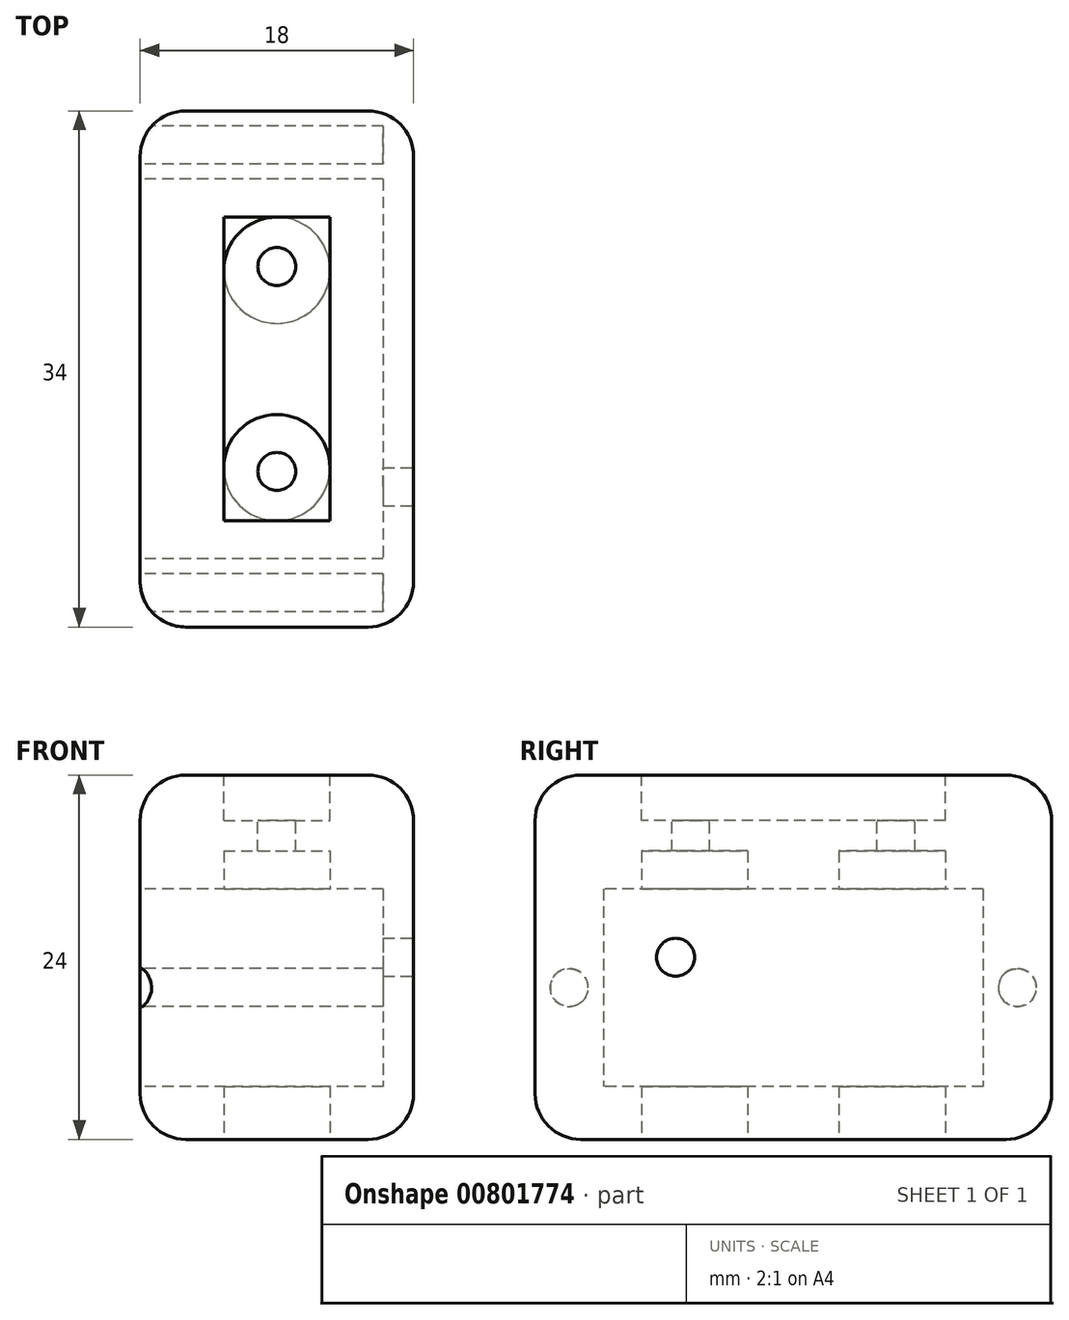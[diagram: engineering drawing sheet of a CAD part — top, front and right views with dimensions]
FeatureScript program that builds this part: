
annotation { "Feature Type Name" : "Feature", "Feature Type Description" : "" }
export const myFeature = defineFeature(function(context is Context, id is Id, definition is map)
    precondition{}
    {
        {
            var Q0;
            Q0=qCreatedBy(makeId("Front.planeOp"),FACE);
            var sketch = newSketch(context, id + "F0", { "sketchPlane" : qUnion([Q0])});
            skLineSegment(sketch, "E0.bottom", {"start": v(-19.6, 6.77) * mm, "end": v(-1.6, 6.77) * mm});
            skLineSegment(sketch, "E0.top", {"start": v(-19.6, -17.23) * mm, "end": v(-1.6, -17.23) * mm});
            skLineSegment(sketch, "E0.left", {"start": v(-19.6, 6.77) * mm, "end": v(-19.6, -17.23) * mm});
            skLineSegment(sketch, "E0.right", {"start": v(-1.6, 6.77) * mm, "end": v(-1.6, -17.23) * mm});
            skSolve(sketch);
        }
        {
            var Q0;
            Q0 = qSketchRegion(id + "F0", true);
            extrude(context, id + "F1", {"entities" : qUnion([Q0]), "depth" : 34 * mm, "offsetDistance" : 25 * mm});
        }
        {
            var Q0;
            Q0=makeQuery(id+"F1.opExtrude","SWEPT_FACE",FACE,{"disambiguationData":[OSD([sQuery(id+"F0.wireOp",EDGE,"E0.left")])]});
            var sketch = newSketch(context, id + "F2", { "sketchPlane" : qUnion([Q0])});
            skLineSegment(sketch, "E1.bottom", {"start": v(4.5, -0.73) * mm, "end": v(29.5, -0.73) * mm});
            skLineSegment(sketch, "E1.top", {"start": v(4.5, -13.73) * mm, "end": v(29.5, -13.73) * mm});
            skLineSegment(sketch, "E1.left", {"start": v(4.5, -0.73) * mm, "end": v(4.5, -13.73) * mm});
            skLineSegment(sketch, "E1.right", {"start": v(29.5, -0.73) * mm, "end": v(29.5, -13.73) * mm});
            skCircle(sketch, "E2", {"center": v(2.25, -7.23) * mm, "radius": 1.25 * mm});
            skPoint(sketch, "E2.centerSnap0", {"position": v(4.5, -7.23) * mm});
            skCircle(sketch, "E3", {"center": v(31.75, -7.23) * mm, "radius": 1.25 * mm});
            skPoint(sketch, "E3.centerSnap0", {"position": v(29.5, -7.23) * mm});
            skSolve(sketch);
        }
        {
            var Q0;
            Q0 = qSketchRegion(id + "F2", true);
            extrude(context, id + "F3", {"entities" : qUnion([Q0]), "operationType" : NewBodyOperationType.REMOVE, "oppositeDirection" : true, "depth" : 16 * mm, "offsetDistance" : 25 * mm});
        }
        {
            var Q0;
            Q0=makeQuery(id+"F1.opExtrude","SWEPT_FACE",FACE,{"disambiguationData":[OSD([sQuery(id+"F0.wireOp",EDGE,"E0.bottom")])]});
            var sketch = newSketch(context, id + "F4", { "sketchPlane" : qUnion([Q0])});
            skLineSegment(sketch, "E4.bottom", {"start": v(-14.1, -7) * mm, "end": v(-7.1, -7) * mm});
            skLineSegment(sketch, "E4.top", {"start": v(-14.1, -27) * mm, "end": v(-7.1, -27) * mm});
            skLineSegment(sketch, "E4.left", {"start": v(-14.1, -7) * mm, "end": v(-14.1, -27) * mm});
            skLineSegment(sketch, "E4.right", {"start": v(-7.1, -7) * mm, "end": v(-7.1, -27) * mm});
            skSolve(sketch);
        }
        {
            var Q0;
            Q0 = qSketchRegion(id + "F4", true);
            extrude(context, id + "F5", {"entities" : qUnion([Q0]), "operationType" : NewBodyOperationType.REMOVE, "oppositeDirection" : true, "depth" : 3 * mm, "offsetDistance" : 25 * mm});
        }
        {
            var Q0;
            Q0=makeQuery(id+"F5.boolean.opBoolean","COPY",FACE,{"derivedFrom":makeQuery(id+"F5.opExtrude","CAP_FACE",FACE,{"disambiguationData":[OSD([sQuery(id+"F4.wireOp",EDGE,"E4.bottom"),sQuery(id+"F4.wireOp",EDGE,"E4.top"),sQuery(id+"F4.wireOp",EDGE,"E4.left"),sQuery(id+"F4.wireOp",EDGE,"E4.right")])],"isStart":false})});
            var sketch = newSketch(context, id + "F6", { "sketchPlane" : qUnion([Q0])});
            skCircle(sketch, "E5", {"center": v(-10.6, -10.25) * mm, "radius": 1.25 * mm});
            skCircle(sketch, "E6", {"center": v(-10.6, -23.75) * mm, "radius": 1.25 * mm});
            skSolve(sketch);
        }
        {
            var Q0;
            Q0 = qSketchRegion(id + "F6", true);
            extrude(context, id + "F7", {"entities" : qUnion([Q0]), "operationType" : NewBodyOperationType.REMOVE, "oppositeDirection" : true, "depth" : 4 * mm, "offsetDistance" : 25 * mm});
        }
        {
            var Q0;
            Q0=makeQuery(id+"F1.opExtrude","SWEPT_EDGE",EDGE,{"disambiguationData":[OSD([sQuery(id+"F0.wireOp",EDGE,"E0.bottom"),sQuery(id+"F0.wireOp",EDGE,"E0.left")])]});
            var Q1;
            Q1=makeQuery(id+"F1.opExtrude","CAP_EDGE",EDGE,{"disambiguationData":[OSD([sQuery(id+"F0.wireOp",EDGE,"E0.left")])],"isStart":false});
            var Q2;
            Q2=makeQuery(id+"F1.opExtrude","CAP_EDGE",EDGE,{"disambiguationData":[OSD([sQuery(id+"F0.wireOp",EDGE,"E0.right")])],"isStart":false});
            var Q3;
            Q3=makeQuery(id+"F1.opExtrude","CAP_EDGE",EDGE,{"disambiguationData":[OSD([sQuery(id+"F0.wireOp",EDGE,"E0.left")])],"isStart":true});
            var Q4;
            Q4=makeQuery(id+"F1.opExtrude","SWEPT_EDGE",EDGE,{"disambiguationData":[OSD([sQuery(id+"F0.wireOp",EDGE,"E0.top"),sQuery(id+"F0.wireOp",EDGE,"E0.left")])]});
            var Q5;
            Q5=makeQuery(id+"F1.opExtrude","CAP_EDGE",EDGE,{"disambiguationData":[OSD([sQuery(id+"F0.wireOp",EDGE,"E0.top")])],"isStart":false});
            var Q6;
            Q6=makeQuery(id+"F1.opExtrude","SWEPT_EDGE",EDGE,{"disambiguationData":[OSD([sQuery(id+"F0.wireOp",EDGE,"E0.top"),sQuery(id+"F0.wireOp",EDGE,"E0.right")])]});
            var Q7;
            Q7=makeQuery(id+"F1.opExtrude","CAP_EDGE",EDGE,{"disambiguationData":[OSD([sQuery(id+"F0.wireOp",EDGE,"E0.right")])],"isStart":true});
            var Q8;
            Q8=makeQuery(id+"F1.opExtrude","CAP_EDGE",EDGE,{"disambiguationData":[OSD([sQuery(id+"F0.wireOp",EDGE,"E0.bottom")])],"isStart":true});
            var Q9;
            Q9=makeQuery(id+"F1.opExtrude","SWEPT_EDGE",EDGE,{"disambiguationData":[OSD([sQuery(id+"F0.wireOp",EDGE,"E0.bottom"),sQuery(id+"F0.wireOp",EDGE,"E0.right")])]});
            var Q10;
            Q10=makeQuery(id+"F1.opExtrude","CAP_EDGE",EDGE,{"disambiguationData":[OSD([sQuery(id+"F0.wireOp",EDGE,"E0.bottom")])],"isStart":false});
            var Q11;
            Q11=makeQuery(id+"F1.opExtrude","CAP_EDGE",EDGE,{"disambiguationData":[OSD([sQuery(id+"F0.wireOp",EDGE,"E0.top")])],"isStart":true});
            fillet(context, id + "F8", {"entities" : qUnion([Q0, Q1, Q2, Q3, Q4, Q5, Q6, Q7, Q8, Q9, Q10, Q11]), "radius" : 3 * mm, "tangentPropagation" : true, "allowEdgeOverflow" : false});
        }
        {
            var Q0;
            Q0=makeQuery(id+"F1.opExtrude","SWEPT_FACE",FACE,{"disambiguationData":[OSD([sQuery(id+"F0.wireOp",EDGE,"E0.top")])]});
            var sketch = newSketch(context, id + "F9", { "sketchPlane" : qUnion([Q0])});
            skCircle(sketch, "E7", {"center": v(-10.6, 10.5) * mm, "radius": 3.5 * mm});
            skCircle(sketch, "E8", {"center": v(-10.6, 23.5) * mm, "radius": 3.5 * mm});
            skSolve(sketch);
        }
        {
            var Q0;
            Q0 = qSketchRegion(id + "F9", true);
            extrude(context, id + "F10", {"entities" : qUnion([Q0]), "operationType" : NewBodyOperationType.REMOVE, "oppositeDirection" : true, "depth" : 19 * mm, "offsetDistance" : 25 * mm});
        }
        {
            var Q0;
            Q0=makeQuery(id+"F1.opExtrude","SWEPT_FACE",FACE,{"disambiguationData":[OSD([sQuery(id+"F0.wireOp",EDGE,"E0.right")])]});
            var sketch = newSketch(context, id + "F11", { "sketchPlane" : qUnion([Q0])});
            skCircle(sketch, "E9", {"center": v(-24.75, -5.23) * mm, "radius": 1.25 * mm});
            skPoint(sketch, "E9.centerSnap0", {"position": v(-3, -5.23) * mm});
            skSolve(sketch);
        }
        {
            var Q0;
            Q0 = qSketchRegion(id + "F11", true);
            extrude(context, id + "F12", {"entities" : qUnion([Q0]), "operationType" : NewBodyOperationType.REMOVE, "endBound" : BoundingType.THROUGH_ALL, "oppositeDirection" : true, "depth" : 25 * mm, "offsetDistance" : 25 * mm});
        }
    });
